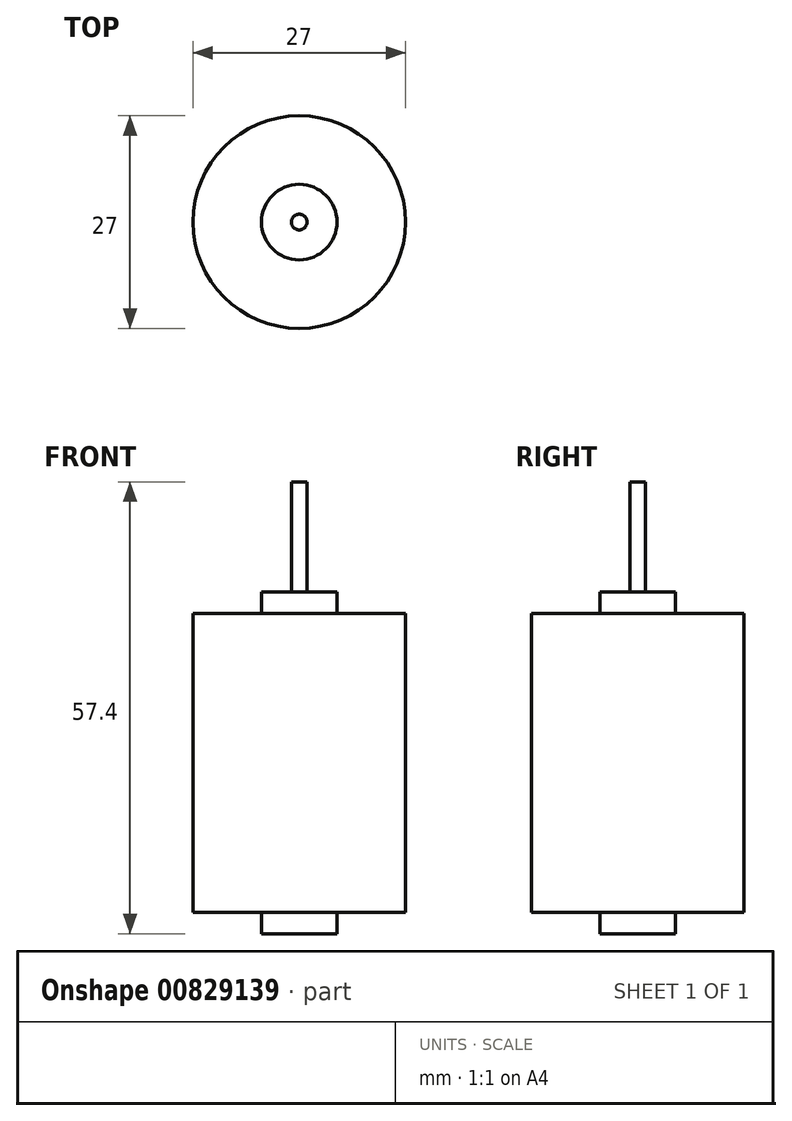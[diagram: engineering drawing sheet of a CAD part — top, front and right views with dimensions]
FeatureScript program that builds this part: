
annotation { "Feature Type Name" : "Feature", "Feature Type Description" : "" }
export const myFeature = defineFeature(function(context is Context, id is Id, definition is map)
    precondition{}
    {
        {
            var Q0;
            Q0=qCreatedBy(makeId("Right.planeOp"),FACE);
            var sketch = newSketch(context, id + "F0", { "sketchPlane" : qUnion([Q0])});
            skLineSegment(sketch, "E0", {"start": v(-4.8, 12.26) * mm, "end": v(-3.8, 12.26) * mm});
            skLineSegment(sketch, "E1", {"start": v(-3.8, 12.26) * mm, "end": v(-3.8, -1.74) * mm});
            skLineSegment(sketch, "E2", {"start": v(-3.8, -1.74) * mm, "end": v(0, -1.74) * mm});
            skLineSegment(sketch, "E3", {"start": v(0, -1.74) * mm, "end": v(0, -4.44) * mm});
            skLineSegment(sketch, "E4", {"start": v(0, -4.44) * mm, "end": v(8.7, -4.44) * mm});
            skLineSegment(sketch, "E5", {"start": v(8.7, -4.44) * mm, "end": v(8.7, -42.44) * mm});
            skLineSegment(sketch, "E6", {"start": v(8.7, -42.44) * mm, "end": v(0, -42.44) * mm});
            skLineSegment(sketch, "E7", {"start": v(0, -42.44) * mm, "end": v(0, -45.14) * mm});
            skLineSegment(sketch, "E8", {"start": v(0, -45.14) * mm, "end": v(-4.8, -45.14) * mm});
            skLineSegment(sketch, "E9", {"start": v(-4.8, -45.14) * mm, "end": v(-4.8, 12.26) * mm});
            skSolve(sketch);
        }
        {
            var Q0;
            Q0=makeQuery(id+"F0.imprint","IMPRINT",FACE,{"disambiguationData":[TD([[makeQuery(id+"F0.imprint","IMPRINT",EDGE,{"derivedFrom":sQuery(id+"F0.wireOp",EDGE,"E0")}),-1.0]])]});
            var Q1;
            Q1=sQuery(id+"F0.wireOp",EDGE,"E9");
            revolve(context, id + "F1", {"surfaceOperationType" : NewSurfaceOperationType.NEW, "entities" : qUnion([Q0]), "axis" : qUnion([Q1]), "revolveType" : RevolveType.FULL});
        }
    });
